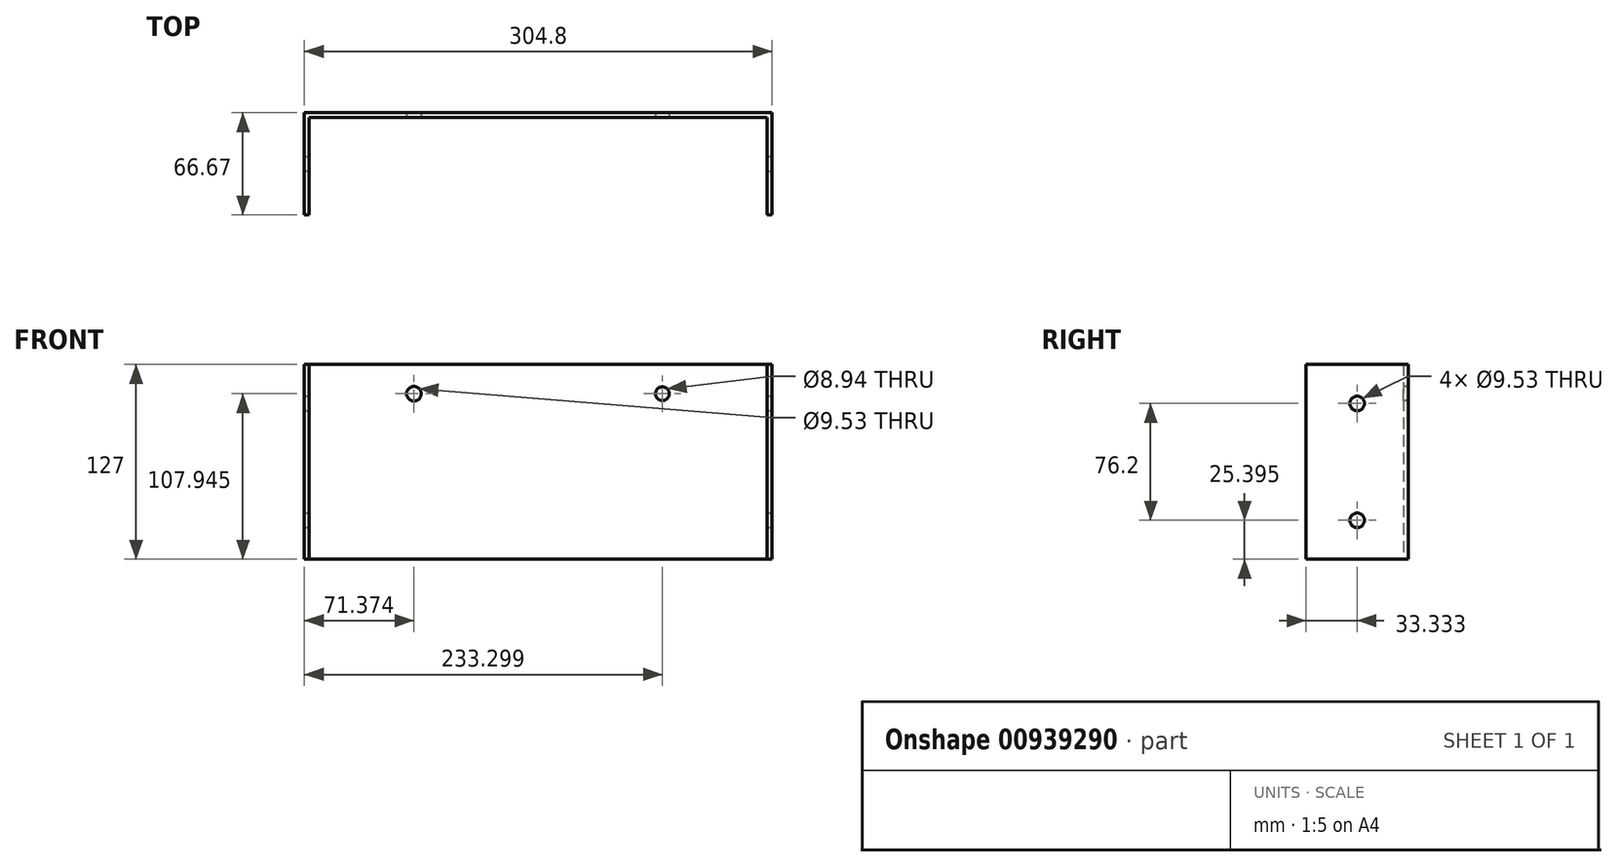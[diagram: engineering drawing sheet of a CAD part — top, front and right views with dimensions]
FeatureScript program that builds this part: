
annotation { "Feature Type Name" : "Feature", "Feature Type Description" : "" }
export const myFeature = defineFeature(function(context is Context, id is Id, definition is map)
    precondition{}
    {
        {
            var Q0;
            Q0=qCreatedBy(makeId("Front.planeOp"),FACE);
            var sketch = newSketch(context, id + "F0", { "sketchPlane" : qUnion([Q0])});
            skLineSegment(sketch, "E0.bottom", {"start": v(-165.41, 59.93) * mm, "end": v(139.39, 59.93) * mm});
            skLineSegment(sketch, "E0.top", {"start": v(-165.41, -67.07) * mm, "end": v(139.39, -67.07) * mm});
            skLineSegment(sketch, "E0.left", {"start": v(-165.41, 59.93) * mm, "end": v(-165.41, -67.07) * mm});
            skLineSegment(sketch, "E0.right", {"start": v(139.39, 59.93) * mm, "end": v(139.39, -67.07) * mm});
            skSolve(sketch);
        }
        {
            var Q0;
            Q0 = qSketchRegion(id + "F0", true);
            extrude(context, id + "F1", {"entities" : qUnion([Q0]), "depth" : 3.17 * mm, "offsetDistance" : 25.4 * mm});
        }
        {
            var Q0;
            Q0=makeQuery(id+"F1.opExtrude","CAP_FACE",FACE,{"disambiguationData":[OSD([sQuery(id+"F0.wireOp",EDGE,"E0.bottom"),sQuery(id+"F0.wireOp",EDGE,"E0.top"),sQuery(id+"F0.wireOp",EDGE,"E0.left"),sQuery(id+"F0.wireOp",EDGE,"E0.right")])],"isStart":false});
            var sketch = newSketch(context, id + "F2", { "sketchPlane" : qUnion([Q0])});
            skLineSegment(sketch, "E1.bottom", {"start": v(-165.41, 59.93) * mm, "end": v(-162.24, 59.93) * mm});
            skLineSegment(sketch, "E1.top", {"start": v(-165.41, -67.07) * mm, "end": v(-162.24, -67.07) * mm});
            skLineSegment(sketch, "E1.left", {"start": v(-165.41, 59.93) * mm, "end": v(-165.41, -67.07) * mm});
            skLineSegment(sketch, "E1.right", {"start": v(-162.24, 59.93) * mm, "end": v(-162.24, -67.07) * mm});
            skLineSegment(sketch, "E2.bottom", {"start": v(139.39, 59.93) * mm, "end": v(136.21, 59.93) * mm});
            skLineSegment(sketch, "E2.top", {"start": v(139.39, -67.07) * mm, "end": v(136.21, -67.07) * mm});
            skLineSegment(sketch, "E2.left", {"start": v(139.39, 59.93) * mm, "end": v(139.39, -67.07) * mm});
            skLineSegment(sketch, "E2.right", {"start": v(136.21, 59.93) * mm, "end": v(136.21, -67.07) * mm});
            skSolve(sketch);
        }
        {
            var Q0;
            Q0 = qSketchRegion(id + "F2", true);
            extrude(context, id + "F3", {"entities" : qUnion([Q0]), "operationType" : NewBodyOperationType.ADD, "depth" : 63.5 * mm, "offsetDistance" : 25.4 * mm});
        }
        {
            var Q0;
            Q0=makeQuery(id+"F1.opExtrude","CAP_FACE",FACE,{"disambiguationData":[OSD([sQuery(id+"F0.wireOp",EDGE,"E0.bottom"),sQuery(id+"F0.wireOp",EDGE,"E0.top"),sQuery(id+"F0.wireOp",EDGE,"E0.left"),sQuery(id+"F0.wireOp",EDGE,"E0.right")])],"isStart":false});
            var sketch = newSketch(context, id + "F4", { "sketchPlane" : qUnion([Q0])});
            skCircle(sketch, "E3", {"center": v(-94.04, 40.88) * mm, "radius": 4.76 * mm});
            skCircle(sketch, "E4", {"center": v(67.89, 40.88) * mm, "radius": 4.47 * mm});
            skSolve(sketch);
        }
        {
            var Q0;
            Q0 = qSketchRegion(id + "F4", true);
            extrude(context, id + "F5", {"entities" : qUnion([Q0]), "operationType" : NewBodyOperationType.REMOVE, "oppositeDirection" : true, "depth" : 25.4 * mm, "offsetDistance" : 25.4 * mm});
        }
        {
            var Q0;
            Q0=makeQuery(id+"F3.boolean.opBoolean","MERGE",FACE,{"derivedFrom":[makeQuery(id+"F1.opExtrude","SWEPT_FACE",FACE,{"disambiguationData":[OSD([sQuery(id+"F0.wireOp",EDGE,"E0.right")])]}),makeQuery(id+"F3.opExtrude","SWEPT_FACE",FACE,{"disambiguationData":[OSD([sQuery(id+"F2.wireOp",EDGE,"E2.left")])]})]});
            var sketch = newSketch(context, id + "F6", { "sketchPlane" : qUnion([Q0])});
            skCircle(sketch, "E5", {"center": v(-33.34, 34.53) * mm, "radius": 4.76 * mm});
            skPoint(sketch, "E5.centerSnap0", {"position": v(-33.34, 59.93) * mm});
            skCircle(sketch, "E6", {"center": v(-33.34, -41.67) * mm, "radius": 4.76 * mm});
            skSolve(sketch);
        }
        {
            var Q0;
            Q0 = qSketchRegion(id + "F6", true);
            extrude(context, id + "F7", {"entities" : qUnion([Q0]), "operationType" : NewBodyOperationType.REMOVE, "oppositeDirection" : true, "depth" : 304.8 * mm, "offsetDistance" : 25.4 * mm});
        }
    });
